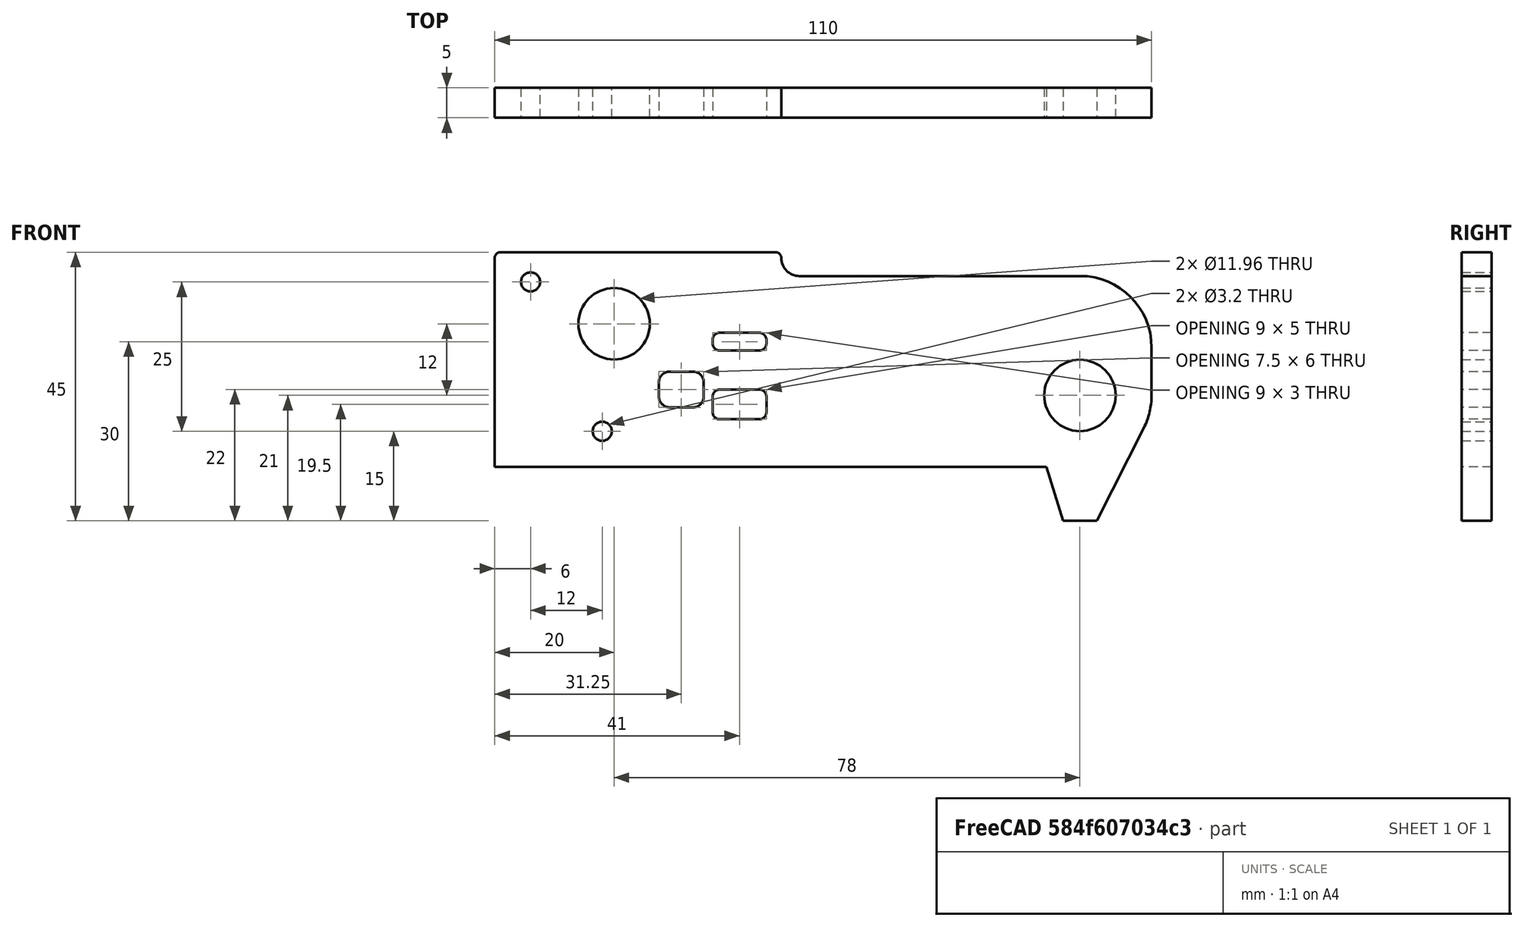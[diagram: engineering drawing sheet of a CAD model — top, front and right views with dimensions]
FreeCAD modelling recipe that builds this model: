
FCSTD DOCUMENT  (FreeCAD 0.17R13541 (Git))
Label: xx_531_y-axis-end-plate
License: All rights reserved
LicenseURL: http://en.wikipedia.org/wiki/All_rights_reserved
objects: Sketcher::SketchObject×1, PartDesign::Pad×1, PartDesign::Body×1
note: 4 computed .brp shape members not serialized (recipe doc carries the construction recipe); baked Part::Feature solids carry a one-line shape summary decoded from their .brp

FEATURE [Sketcher::SketchObject] Sketch041
  MapMode = 5
  Placement = pos=(0,0,0) rot=(1,0,0;1.5708rad)
  Support = -> [XZ_Plane]
  sketch-geometry (44):
    g0: Circle CenterX=-14 CenterY=7 CenterZ=0 NormalX=0 NormalY=0 NormalZ=-1 AngleXU=0 Radius=1.6
    g1: LineSegment StartX=75.17 StartY=-33 StartZ=0 EndX=80.83 EndY=-33 EndZ=0
    g2: LineSegment StartX=-20 StartY=-24 StartZ=0 EndX=72.36 EndY=-24 EndZ=0
    g3: ArcOfCircle CenterX=78 CenterY=-4 CenterZ=0 NormalX=0 NormalY=0 NormalZ=1 AngleXU=0 Radius=12 StartAngle=0 EndAngle=1.5708
    g4: ArcOfCircle CenterX=9.3 CenterY=-12.2 CenterZ=0 NormalX=0 NormalY=0 NormalZ=1 AngleXU=0 Radius=1.8 StartAngle=3.14159 EndAngle=4.71239
    g5: LineSegment StartX=17.7 StartY=-4.5 StartZ=0 EndX=24.3 EndY=-4.5 EndZ=0
    g6: LineSegment StartX=17.7 StartY=-16 StartZ=0 EndX=24.3 EndY=-16 EndZ=0
    g7: LineSegment StartX=13.2 StartY=-8 StartZ=0 EndX=9.3 EndY=-8 EndZ=0
    g8: Circle CenterX=-2 CenterY=-18 CenterZ=0 NormalX=0 NormalY=0 NormalZ=-1 AngleXU=0 Radius=1.6
    g9: Circle CenterX=0 CenterY=0 CenterZ=0 NormalX=0 NormalY=0 NormalZ=-1 AngleXU=0 Radius=5.98
    g10: Circle CenterX=78 CenterY=-12 CenterZ=0 NormalX=0 NormalY=0 NormalZ=-1 AngleXU=0 Radius=5.98
    g11: ArcOfCircle CenterX=13.2 CenterY=-12.2 CenterZ=0 NormalX=0 NormalY=0 NormalZ=1 AngleXU=0 Radius=1.8 StartAngle=4.71239 EndAngle=6.28319
    g12: ArcOfCircle CenterX=27 CenterY=11 CenterZ=0 NormalX=0 NormalY=0 NormalZ=1 AngleXU=0 Radius=1 StartAngle=0 EndAngle=1.5708
    g13: LineSegment StartX=80.83 StartY=-33 StartZ=0 EndX=88.7093 EndY=-17.4139 EndZ=0
    g14: LineSegment StartX=25.5 StartY=-3.3 StartZ=0 EndX=25.5 EndY=-2.7 EndZ=0
    g15: ArcOfCircle CenterX=31 CenterY=11 CenterZ=0 NormalX=0 NormalY=0 NormalZ=1 AngleXU=0 Radius=3 StartAngle=3.14159 EndAngle=4.71239
    g16: LineSegment StartX=24.3 StartY=-11 StartZ=0 EndX=17.7 EndY=-11 EndZ=0
    g17: ArcOfCircle CenterX=17.7 CenterY=-12.2 CenterZ=0 NormalX=0 NormalY=0 NormalZ=1 AngleXU=0 Radius=1.2 StartAngle=1.5708 EndAngle=3.14159
    g18: LineSegment StartX=25.5 StartY=-14.8 StartZ=0 EndX=25.5 EndY=-12.2 EndZ=0
    g19: ArcOfCircle CenterX=24.3 CenterY=-2.7 CenterZ=0 NormalX=0 NormalY=0 NormalZ=1 AngleXU=0 Radius=1.2 StartAngle=0 EndAngle=1.5708
    g20: ArcOfCircle CenterX=13.2 CenterY=-9.8 CenterZ=0 NormalX=0 NormalY=0 NormalZ=1 AngleXU=0 Radius=1.8 StartAngle=0 EndAngle=1.5708
    g21: LineSegment StartX=7.5 StartY=-9.8 StartZ=0 EndX=7.5 EndY=-12.2 EndZ=0
    g22: ArcOfCircle CenterX=24.3 CenterY=-3.3 CenterZ=0 NormalX=0 NormalY=0 NormalZ=1 AngleXU=0 Radius=1.2 StartAngle=4.71239 EndAngle=6.28319
    g23: ArcOfCircle CenterX=78 CenterY=-12 CenterZ=0 NormalX=0 NormalY=0 NormalZ=1 AngleXU=0 Radius=12 StartAngle=5.81512 EndAngle=6.28319
    g24: LineSegment StartX=-20 StartY=11 StartZ=0 EndX=-20 EndY=-24 EndZ=0
    g25: LineSegment StartX=24.3 StartY=-1.5 StartZ=0 EndX=17.7 EndY=-1.5 EndZ=0
    g26: ArcOfCircle CenterX=24.3 CenterY=-14.8 CenterZ=0 NormalX=0 NormalY=0 NormalZ=1 AngleXU=0 Radius=1.2 StartAngle=4.71239 EndAngle=6.28319
    g27: LineSegment StartX=9.3 StartY=-14 StartZ=0 EndX=13.2 EndY=-14 EndZ=0
    g28: LineSegment StartX=27 StartY=12 StartZ=0 EndX=-19 EndY=12 EndZ=0
    g29: ArcOfCircle CenterX=-19 CenterY=11 CenterZ=0 NormalX=0 NormalY=0 NormalZ=1 AngleXU=0 Radius=1 StartAngle=1.5708 EndAngle=3.14159
    g30: LineSegment StartX=16.5 StartY=-12.2 StartZ=0 EndX=16.5 EndY=-14.8 EndZ=0
    g31: ArcOfCircle CenterX=17.7 CenterY=-3.3 CenterZ=0 NormalX=0 NormalY=0 NormalZ=1 AngleXU=0 Radius=1.2 StartAngle=3.14159 EndAngle=4.71239
    g32: LineSegment StartX=15 StartY=-12.2 StartZ=0 EndX=15 EndY=-9.8 EndZ=0
    g33: ArcOfCircle CenterX=24.3 CenterY=-12.2 CenterZ=0 NormalX=0 NormalY=0 NormalZ=1 AngleXU=0 Radius=1.2 StartAngle=0 EndAngle=1.5708
    g34: ArcOfCircle CenterX=9.3 CenterY=-9.8 CenterZ=0 NormalX=0 NormalY=0 NormalZ=1 AngleXU=0 Radius=1.8 StartAngle=1.5708 EndAngle=3.14159
    g35: LineSegment StartX=90 StartY=-12 StartZ=0 EndX=90 EndY=-4 EndZ=0
    g36: LineSegment StartX=16.5 StartY=-2.7 StartZ=0 EndX=16.5 EndY=-3.3 EndZ=0
    g37: LineSegment StartX=78 StartY=8 StartZ=0 EndX=31 EndY=8 EndZ=0
    g38: LineSegment StartX=72.36 StartY=-24 StartZ=0 EndX=75.17 EndY=-33 EndZ=0
    g39: ArcOfCircle CenterX=17.7 CenterY=-2.7 CenterZ=0 NormalX=0 NormalY=0 NormalZ=1 AngleXU=0 Radius=1.2 StartAngle=1.5708 EndAngle=3.14159
    g40: ArcOfCircle CenterX=17.7 CenterY=-14.8 CenterZ=0 NormalX=0 NormalY=0 NormalZ=1 AngleXU=0 Radius=1.2 StartAngle=3.14159 EndAngle=4.71239
    g41: LineSegment [constr] StartX=78 StartY=8 StartZ=0 EndX=78 EndY=-33 EndZ=0
    g42: LineSegment [constr] StartX=78 StartY=-12 StartZ=0 EndX=90 EndY=-12 EndZ=0
    g43: LineSegment [constr] StartX=31 StartY=11 StartZ=0 EndX=27 EndY=11 EndZ=0
  constraints (116):
    c: Radius(g29) = 1
    c: Equal(g29,g12)
    c: Radius(g40) = 1.2
    c: Equal(g40,g17)
    c: Equal(g40,g26)
    c: Equal(g40,g33)
    c: Equal(g40,g31)
    c: Equal(g40,g39)
    c: Equal(g40,g22)
    c: Equal(g40,g19)
    c: Equal(g4,g11)
    c: Equal(g11,g20)
    c: Equal(g20,g34)
    c: Radius(g4) = 1.8
    c: Equal(g8,g0)
    c: Radius(g0) = 1.6
    c: Radius(g9) = 5.98
    c: Coincident(g-1,g9)
    c: DistanceX(g-1,g10) = 78
    c: DistanceY(g10,g-1) = 12
    c: Equal(g9,g10)
    c: DistanceX(g-2,g0) = -14
    c: DistanceY(g-1,g0) = 7
    c: DistanceY(g8,g0) = 25
    c: DistanceX(g0,g8) = 12
    c: Distance(g7,g27) = 6
    c: Distance(g20,g21) = 7.5
    c: DistanceX(g-2,g21) = 7.5
    c: DistanceY(g-1,g4) = -14
    c: DistanceX(g-2,g30) = 16.5
    c: DistanceY(g-1,g6) = -16
    c: Distance(g18,g30) = 9
    c: Distance(g16,g6) = 5
    c: PointOnObject(g31,g30)
    c: PointOnObject(g14,g18)
    c: Distance(g5,g6) = 11.5
    c: Distance(g25,g5) = 3
    c: Distance(g1) = 5.66
    c: Tangent(g30,g17)
    c: Coincident(g2,g24)
    c: Coincident(g30,g17)
    c: Coincident(g38,g2)
    c: Coincident(g38,g1)
    c: Tangent(g25,g39) = -1.5708
    c: Tangent(g36,g39) = -1.5708
    c: Tangent(g31,g36) = -1.5708
    c: Tangent(g5,g31) = -1.5708
    c: Tangent(g19,g25) = -1.5708
    c: Tangent(g14,g19) = -1.5708
    c: Tangent(g14,g22) = -1.5708
    c: Tangent(g5,g22) = -1.5708
    c: Tangent(g16,g17) = -1.5708
    c: Tangent(g16,g33) = -1.5708
    c: Tangent(g18,g33) = -1.5708
    c: Tangent(g18,g26) = -1.5708
    c: Tangent(g6,g26) = -1.5708
    c: Tangent(g6,g40) = -1.5708
    c: Tangent(g30,g40) = -1.5708
    c: Tangent(g7,g20) = -1.5708
    c: Tangent(g20,g32) = -1.5708
    c: Tangent(g11,g32) = -1.5708
    c: Tangent(g11,g27) = -1.5708
    c: Tangent(g4,g27) = -1.5708
    c: Tangent(g4,g21) = -1.5708
    c: Tangent(g21,g34) = -1.5708
    c: Tangent(g7,g34) = -1.5708
    c: Tangent(g28,g29) = -1.5708
    c: Tangent(g24,g29) = -1.5708
    c: Tangent(g29,g28) = -1.5708
    c: Tangent(g28,g12) = -1.5708
    c: Tangent(g15,g12) = 1.5708
    c: Tangent(g15,g37) = 1.5708
    c: Tangent(g3,g37) = -1.5708
    c: Tangent(g3,g35) = -1.5708
    c: Tangent(g35,g23) = -1.5708
    c: Tangent(g13,g23) = -1.5708
    c: Horizontal(g2)
    c: Horizontal(g27)
    c: Horizontal(g7)
    c: Horizontal(g6)
    c: Horizontal(g16)
    c: Horizontal(g5)
    c: Horizontal(g25)
    c: Horizontal(g28)
    c: Horizontal(g37)
    c: Horizontal(g1)
    c: Vertical(g24)
    c: Vertical(g35)
    c: Vertical(g21)
    c: Vertical(g32)
    c: Vertical(g30)
    c: Vertical(g18)
    c: Vertical(g14)
    c: Vertical(g36)
    c: DistanceY(g-1,g28) = 12
    c: DistanceY(g-1,g2) = -24
    c: DistanceX(g-2,g2) = -20
    c: DistanceX(g-2,g12) = 28
    c: PointOnObject(g10,g41)
    c: Vertical(g41)
    c: Coincident(g41,g3)
    c: Coincident(g1,g13)
    c: DistanceY(g-1,g1) = -33
    c: PointOnObject(g41,g1)
    c: Symmetric(g1,g1,g41)
    c: Equal(g23,g3)
    c: DistanceY(g-1,g3) = 8
    c: DistanceX(g-2,g3) = 90
    c: Distance(g35) = 8
    c: Coincident(g42,g10)
    c: Horizontal(g42)
    c: Coincident(g42,g23)
    c: Distance(g2,g41) = 5.64
    c: Coincident(g43,g12)
    c: Coincident(g43,g15)
    c: Horizontal(g43)
FEATURE [PartDesign::Pad] Pad
  Length = 5
  Length2 = 100
  Placement = pos=(0,0,0) rot=(1,0,0;1.5708rad)
  Profile = -> Sketch041
  Type = 0
FEATURE [PartDesign::Body] Body
  Group = -> [Sketch041,Pad]
  Origin = -> Origin
  Tip = -> Pad
